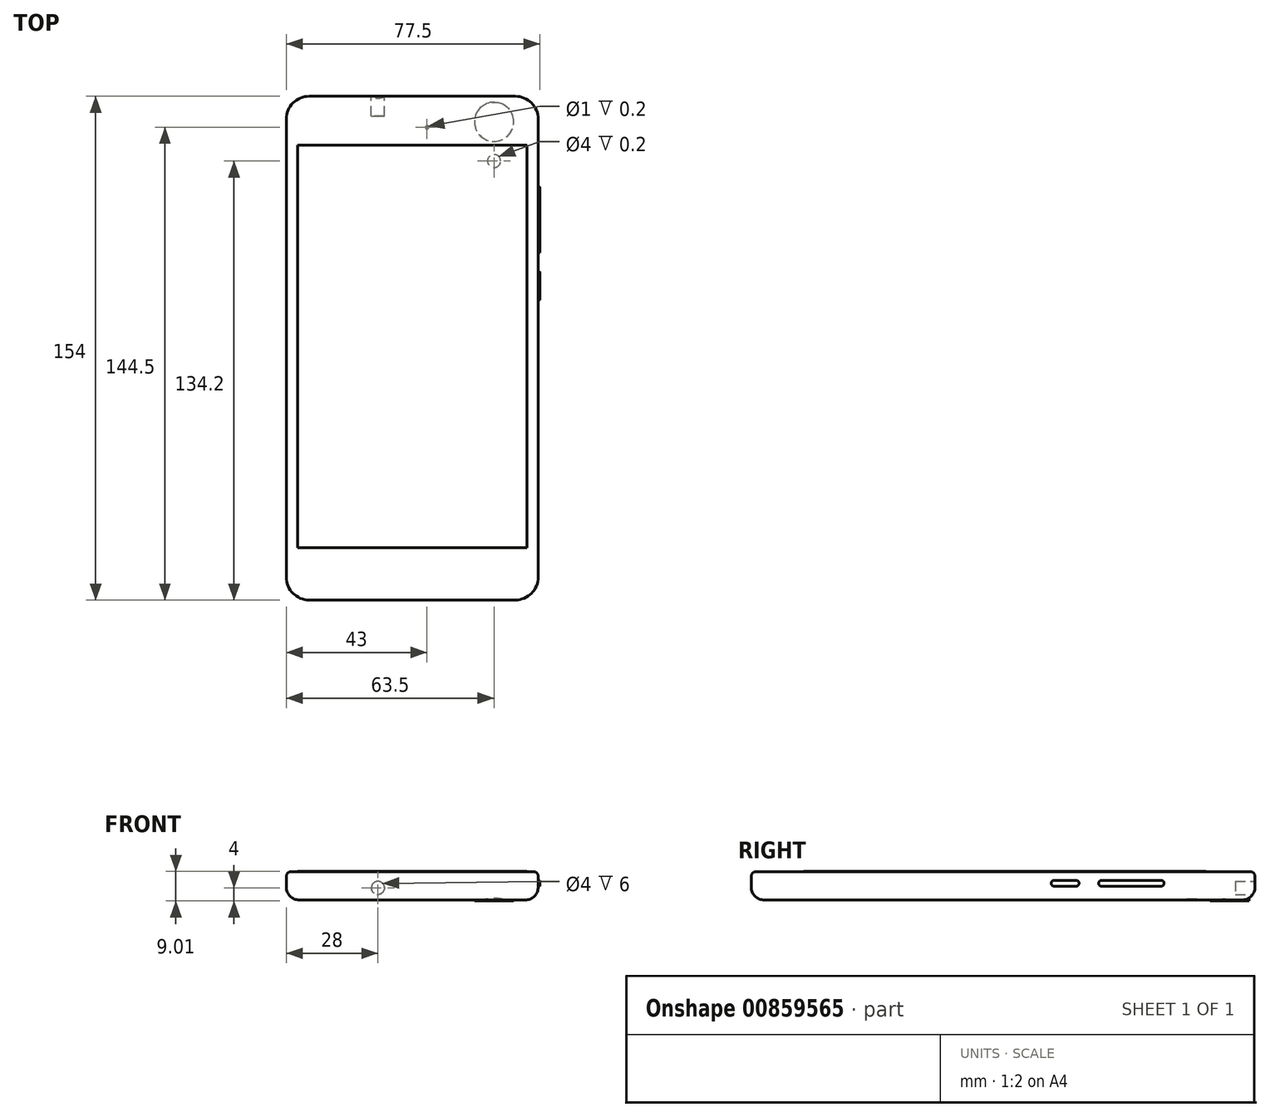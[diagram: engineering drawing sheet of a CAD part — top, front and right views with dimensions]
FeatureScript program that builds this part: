
annotation { "Feature Type Name" : "Feature", "Feature Type Description" : "" }
export const myFeature = defineFeature(function(context is Context, id is Id, definition is map)
    precondition{}
    {
        {
            var Q0;
            Q0=qCreatedBy(makeId("Top.planeOp"),FACE);
            var sketch = newSketch(context, id + "F0", { "sketchPlane" : qUnion([Q0])});
            skLineSegment(sketch, "E0.bottom", {"start": v(-31.5, 77) * mm, "end": v(31.5, 77) * mm});
            skLineSegment(sketch, "E0.top", {"start": v(-31.5, -77) * mm, "end": v(31.5, -77) * mm});
            skLineSegment(sketch, "E0.left", {"start": v(-38.5, 70) * mm, "end": v(-38.5, -70) * mm});
            skLineSegment(sketch, "E0.right", {"start": v(38.5, 70) * mm, "end": v(38.5, -70) * mm});
            skPoint(sketch, "E1.visualSharp", {"position": v(-38.5, 77) * mm});
            skArc(sketch, "E1.filletArc", {"start": v(-31.5, 77) * mm, "mid": v(-36.45, 74.95) * mm, "end": v(-38.5, 70) * mm});
            skPoint(sketch, "E2.visualSharp", {"position": v(-38.5, -77) * mm});
            skArc(sketch, "E2.filletArc", {"start": v(-38.5, -70) * mm, "mid": v(-36.45, -74.95) * mm, "end": v(-31.5, -77) * mm});
            skPoint(sketch, "E3.visualSharp", {"position": v(38.5, -77) * mm});
            skArc(sketch, "E3.filletArc", {"start": v(31.5, -77) * mm, "mid": v(36.45, -74.95) * mm, "end": v(38.5, -70) * mm});
            skPoint(sketch, "E4.visualSharp", {"position": v(38.5, 77) * mm});
            skArc(sketch, "E4.filletArc", {"start": v(38.5, 70) * mm, "mid": v(36.45, 74.95) * mm, "end": v(31.5, 77) * mm});
            skLineSegment(sketch, "E5", {"start": v(-38.5, 77) * mm, "end": v(38.5, -77) * mm, "construction": true});
            skSolve(sketch);
        }
        {
            var Q0;
            Q0=makeQuery(id+"F0.imprint","IMPRINT",FACE,{"disambiguationData":[TD([[makeQuery(id+"F0.imprint","IMPRINT",EDGE,{"derivedFrom":sQuery(id+"F0.wireOp",EDGE,"E0.bottom")}),-1.0]])]});
            extrude(context, id + "F1", {"entities" : qUnion([Q0]), "depth" : 8.7 * mm, "offsetDistance" : 25 * mm, "symmetric" : true});
        }
        {
            var Q0;
            Q0=makeQuery(id+"F1.opExtrude","CAP_EDGE",EDGE,{"disambiguationData":[OSD([sQuery(id+"F0.wireOp",EDGE,"E0.right")])],"isStart":true});
            fillet(context, id + "F2", {"entities" : qUnion([Q0]), "radius" : 4 * mm, "tangentPropagation" : true, "allowEdgeOverflow" : false});
        }
        {
            var Q0;
            Q0=makeQuery(id+"F1.opExtrude","CAP_FACE",FACE,{"disambiguationData":[OSD([sQuery(id+"F0.wireOp",EDGE,"E0.bottom"),sQuery(id+"F0.wireOp",EDGE,"E0.top"),sQuery(id+"F0.wireOp",EDGE,"E0.left"),sQuery(id+"F0.wireOp",EDGE,"E0.right"),sQuery(id+"F0.wireOp",EDGE,"E1.filletArc"),sQuery(id+"F0.wireOp",EDGE,"E2.filletArc"),sQuery(id+"F0.wireOp",EDGE,"E3.filletArc"),sQuery(id+"F0.wireOp",EDGE,"E4.filletArc")])],"isStart":false});
            fillet(context, id + "F3", {"entities" : qUnion([Q0]), "radius" : 1.5 * mm, "tangentPropagation" : true, "allowEdgeOverflow" : false});
        }
        {
            var Q0;
            Q0=makeQuery(id+"F1.opExtrude","CAP_FACE",FACE,{"disambiguationData":[OSD([sQuery(id+"F0.wireOp",EDGE,"E0.bottom"),sQuery(id+"F0.wireOp",EDGE,"E0.top"),sQuery(id+"F0.wireOp",EDGE,"E0.left"),sQuery(id+"F0.wireOp",EDGE,"E0.right"),sQuery(id+"F0.wireOp",EDGE,"E1.filletArc"),sQuery(id+"F0.wireOp",EDGE,"E2.filletArc"),sQuery(id+"F0.wireOp",EDGE,"E3.filletArc"),sQuery(id+"F0.wireOp",EDGE,"E4.filletArc")])],"isStart":true});
            cPlane(context, id + "F4", {"entities" : qUnion([Q0]), "cplaneType" : CPlaneType.OFFSET, "offset" : 0.3 * mm, "width" : 150 * mm, "height" : 150 * mm});
        }
        {
            var Q0;
            Q0=makeQuery(id+"F1.opExtrude","CAP_FACE",FACE,{"disambiguationData":[OSD([sQuery(id+"F0.wireOp",EDGE,"E0.bottom"),sQuery(id+"F0.wireOp",EDGE,"E0.top"),sQuery(id+"F0.wireOp",EDGE,"E0.left"),sQuery(id+"F0.wireOp",EDGE,"E0.right"),sQuery(id+"F0.wireOp",EDGE,"E1.filletArc"),sQuery(id+"F0.wireOp",EDGE,"E2.filletArc"),sQuery(id+"F0.wireOp",EDGE,"E3.filletArc"),sQuery(id+"F0.wireOp",EDGE,"E4.filletArc")])],"isStart":false});
            var sketch = newSketch(context, id + "F5", { "sketchPlane" : qUnion([Q0])});
            skLineSegment(sketch, "E6.0", {"start": v(-38.5, -70) * mm, "end": v(-38.5, 70) * mm});
            skLineSegment(sketch, "E7.0", {"start": v(31.5, -77) * mm, "end": v(-31.5, -77) * mm});
            skLineSegment(sketch, "E8.0", {"start": v(38.5, 70) * mm, "end": v(38.5, -70) * mm});
            skLineSegment(sketch, "E9.0", {"start": v(-31.5, 77) * mm, "end": v(31.5, 77) * mm});
            skSolve(sketch);
        }
        {
            var Q0;
            Q0=makeQuery(id+"F1.opExtrude","CAP_FACE",FACE,{"disambiguationData":[OSD([sQuery(id+"F0.wireOp",EDGE,"E0.bottom"),sQuery(id+"F0.wireOp",EDGE,"E0.top"),sQuery(id+"F0.wireOp",EDGE,"E0.left"),sQuery(id+"F0.wireOp",EDGE,"E0.right"),sQuery(id+"F0.wireOp",EDGE,"E1.filletArc"),sQuery(id+"F0.wireOp",EDGE,"E2.filletArc"),sQuery(id+"F0.wireOp",EDGE,"E3.filletArc"),sQuery(id+"F0.wireOp",EDGE,"E4.filletArc")])],"isStart":true});
            var sketch = newSketch(context, id + "F6", { "sketchPlane" : qUnion([Q0])});
            skLineSegment(sketch, "E10.0", {"start": v(31.5, -77) * mm, "end": v(-31.5, -77) * mm});
            skLineSegment(sketch, "E11.0", {"start": v(38.5, 70) * mm, "end": v(38.5, -70) * mm});
            skLineSegment(sketch, "E12", {"start": v(38.5, -70) * mm, "end": v(38.5, -77) * mm, "construction": true});
            skLineSegment(sketch, "E13", {"start": v(38.5, -77) * mm, "end": v(31.5, -77) * mm, "construction": true});
            skSolve(sketch);
        }
        {
            var Q0;
            Q0=qCreatedBy(id+"F4.planeOp",FACE);
            var sketch = newSketch(context, id + "F7", { "sketchPlane" : qUnion([Q0])});
            skCircle(sketch, "E14", {"center": v(25, -69.2) * mm, "radius": 6 * mm});
            skSolve(sketch);
        }
        {
            var Q0;
            Q0=makeQuery(id+"F7.imprint","IMPRINT",FACE,{"disambiguationData":[TD([[makeQuery(id+"F7.imprint","IMPRINT",EDGE,{"derivedFrom":sQuery(id+"F7.wireOp",EDGE,"E14")}),1.0]])]});
            var Q1;
            Q1=qCreatedBy(makeId("Top.planeOp"),FACE);
            extrude(context, id + "F8", {"entities" : qUnion([Q0]), "operationType" : NewBodyOperationType.ADD, "endBound" : BoundingType.UP_TO_SURFACE, "oppositeDirection" : true, "depth" : 25 * mm, "endBoundEntityFace" : qUnion([Q1]), "offsetDistance" : 25 * mm});
        }
        {
            var Q0;
            {var subQ0=sQuery(id+"F0.wireOp",EDGE,"E4.filletArc");var subQ1=sQuery(id+"F0.wireOp",EDGE,"E3.filletArc");var subQ2=sQuery(id+"F0.wireOp",EDGE,"E2.filletArc");var subQ3=sQuery(id+"F0.wireOp",EDGE,"E1.filletArc");var subQ4=sQuery(id+"F0.wireOp",EDGE,"E0.right");var subQ5=sQuery(id+"F0.wireOp",EDGE,"E0.left");var subQ6=sQuery(id+"F0.wireOp",EDGE,"E0.top");var subQ7=sQuery(id+"F0.wireOp",EDGE,"E0.bottom");var subQ8=makeQuery(id+"F1.opExtrude","CAP_FACE",FACE,{"disambiguationData":[OSD([subQ7,subQ6,subQ5,subQ4,subQ3,subQ2,subQ1,subQ0])],"isStart":false});Q0=makeQuery(id+"F5.imprint","IMPRINT",FACE,{"disambiguationData":[TD([[makeQuery(id+"F5.imprint","IMPRINT",EDGE,{"derivedFrom":makeQuery(id+"F3.opFillet","BLEND_EDGE",EDGE,{"blendedFrom":[makeQuery(id+"F1.opExtrude","CAP_EDGE",EDGE,{"disambiguationData":[OSD([subQ7])],"isStart":false}),subQ8],"blendedInto":[subQ8]})}),1.0]])]});}
            var sketch = newSketch(context, id + "F9", { "sketchPlane" : qUnion([Q0])});
            skLineSegment(sketch, "E15.bottom", {"start": v(-35.1, 62) * mm, "end": v(35.1, 62) * mm});
            skLineSegment(sketch, "E15.top", {"start": v(-35.1, -61) * mm, "end": v(35.1, -61) * mm});
            skLineSegment(sketch, "E15.left", {"start": v(-35.1, 62) * mm, "end": v(-35.1, -61) * mm});
            skLineSegment(sketch, "E15.right", {"start": v(35.1, 62) * mm, "end": v(35.1, -61) * mm});
            skSolve(sketch);
        }
        {
            var Q0;
            Q0=makeQuery(id+"F9.imprint","IMPRINT",FACE,{"disambiguationData":[TD([[makeQuery(id+"F9.imprint","IMPRINT",EDGE,{"derivedFrom":sQuery(id+"F9.wireOp",EDGE,"E15.bottom")}),-1.0]])]});
            var Q1;
            Q1=sQuery(id+"F9.wireOp",EDGE,"E15.bottom");
            var Q2;
            Q2=sQuery(id+"F9.wireOp",EDGE,"E15.left");
            var Q3;
            Q3=sQuery(id+"F9.wireOp",EDGE,"E15.top");
            var Q4;
            Q4=sQuery(id+"F9.wireOp",EDGE,"E15.right");
            extrude(context, id + "F10", {"entities" : qUnion([Q0]), "surfaceOperationType" : NewSurfaceOperationType.ADD, "surfaceEntities" : qUnion([Q1, Q2, Q3, Q4]), "depth" : 0.01 * mm, "offsetDistance" : 25 * mm});
        }
        {
            var Q0;
            {var subQ0=sQuery(id+"F0.wireOp",EDGE,"E4.filletArc");var subQ1=sQuery(id+"F0.wireOp",EDGE,"E3.filletArc");var subQ2=sQuery(id+"F0.wireOp",EDGE,"E2.filletArc");var subQ3=sQuery(id+"F0.wireOp",EDGE,"E1.filletArc");var subQ4=sQuery(id+"F0.wireOp",EDGE,"E0.right");var subQ5=sQuery(id+"F0.wireOp",EDGE,"E0.left");var subQ6=sQuery(id+"F0.wireOp",EDGE,"E0.top");var subQ7=sQuery(id+"F0.wireOp",EDGE,"E0.bottom");var subQ8=makeQuery(id+"F1.opExtrude","CAP_FACE",FACE,{"disambiguationData":[OSD([subQ7,subQ6,subQ5,subQ4,subQ3,subQ2,subQ1,subQ0])],"isStart":true});Q0=makeQuery(id+"F6.imprint","IMPRINT",FACE,{"disambiguationData":[TD([[makeQuery(id+"F6.imprint","IMPRINT",EDGE,{"derivedFrom":makeQuery(id+"F2.opFillet","BLEND_EDGE",EDGE,{"blendedFrom":[makeQuery(id+"F1.opExtrude","CAP_EDGE",EDGE,{"disambiguationData":[OSD([subQ7])],"isStart":true}),subQ8],"blendedInto":[subQ8]})}),1.0]])]});}
            var sketch = newSketch(context, id + "F11", { "sketchPlane" : qUnion([Q0])});
            skCircle(sketch, "E16", {"center": v(25, -57.2) * mm, "radius": 2 * mm});
            skCircle(sketch, "E17.0", {"center": v(25, -69.2) * mm, "radius": 6 * mm});
            skCircle(sketch, "E18", {"center": v(4.5, -67.5) * mm, "radius": 0.5 * mm});
            skSolve(sketch);
        }
        {
            var Q0;
            Q0=makeQuery(id+"F11.imprint","IMPRINT",FACE,{"disambiguationData":[TD([[makeQuery(id+"F11.imprint","IMPRINT",EDGE,{"derivedFrom":sQuery(id+"F11.wireOp",EDGE,"E16")}),1.0]])]});
            var Q1;
            Q1=makeQuery(id+"F11.imprint","IMPRINT",FACE,{"disambiguationData":[TD([[makeQuery(id+"F11.imprint","IMPRINT",EDGE,{"derivedFrom":sQuery(id+"F11.wireOp",EDGE,"E18")}),1.0]])]});
            extrude(context, id + "F12", {"entities" : qUnion([Q0, Q1]), "operationType" : NewBodyOperationType.REMOVE, "oppositeDirection" : true, "depth" : 0.2 * mm, "offsetDistance" : 25 * mm});
        }
        {
            var Q0;
            Q0=makeQuery(id+"F1.opExtrude","SWEPT_FACE",FACE,{"disambiguationData":[OSD([sQuery(id+"F0.wireOp",EDGE,"E0.bottom")])]});
            var sketch = newSketch(context, id + "F13", { "sketchPlane" : qUnion([Q0])});
            skCircle(sketch, "E19", {"center": v(10.5, -0.65) * mm, "radius": 2 * mm});
            skSolve(sketch);
        }
        {
            var Q0;
            {var subQ0=sQuery(id+"F13.wireOp",EDGE,"E19");var subQ1=sQuery(id+"F0.wireOp",EDGE,"E0.bottom");var subQ2=makeQuery(id+"F2.opFillet","BLEND_EDGE",EDGE,{"blendedFrom":[makeQuery(id+"F1.opExtrude","CAP_EDGE",EDGE,{"disambiguationData":[OSD([subQ1])],"isStart":true}),makeQuery(id+"F1.opExtrude","SWEPT_FACE",FACE,{"disambiguationData":[OSD([subQ1])]})],"blendedInto":[makeQuery(id+"F1.opExtrude","SWEPT_FACE",FACE,{"disambiguationData":[OSD([subQ1])]})]});var subQ3=makeQuery(id+"F13.imprint","INTERSECT",VERTEX,{"disambiguationData":[OD(0.0)],"derivedFrom":[subQ2,subQ0]});Q0=makeQuery(id+"F13.imprint","IMPRINT",FACE,{"disambiguationData":[TD([[makeQuery(id+"F13.imprint","IMPRINT",EDGE,{"disambiguationData":[TD([[subQ3,-1.0]])],"derivedFrom":subQ0}),1.0]])]});}
            var Q1;
            {var subQ0=sQuery(id+"F13.wireOp",EDGE,"E19");var subQ1=sQuery(id+"F0.wireOp",EDGE,"E0.bottom");var subQ2=makeQuery(id+"F2.opFillet","BLEND_EDGE",EDGE,{"blendedFrom":[makeQuery(id+"F1.opExtrude","CAP_EDGE",EDGE,{"disambiguationData":[OSD([subQ1])],"isStart":true}),makeQuery(id+"F1.opExtrude","SWEPT_FACE",FACE,{"disambiguationData":[OSD([subQ1])]})],"blendedInto":[makeQuery(id+"F1.opExtrude","SWEPT_FACE",FACE,{"disambiguationData":[OSD([subQ1])]})]});var subQ3=makeQuery(id+"F13.imprint","INTERSECT",VERTEX,{"disambiguationData":[OD(0.0)],"derivedFrom":[subQ2,subQ0]});Q1=makeQuery(id+"F13.imprint","IMPRINT",FACE,{"disambiguationData":[TD([[makeQuery(id+"F13.imprint","IMPRINT",EDGE,{"disambiguationData":[TD([[subQ3,1.0]])],"derivedFrom":subQ0}),1.0]])]});}
            extrude(context, id + "F14", {"entities" : qUnion([Q0, Q1]), "operationType" : NewBodyOperationType.REMOVE, "oppositeDirection" : true, "depth" : 6 * mm, "offsetDistance" : 25 * mm});
        }
        {
            var Q0;
            Q0=makeQuery(id+"F1.opExtrude","SWEPT_FACE",FACE,{"disambiguationData":[OSD([sQuery(id+"F0.wireOp",EDGE,"E0.right")])]});
            var sketch = newSketch(context, id + "F15", { "sketchPlane" : qUnion([Q0])});
            skLineSegment(sketch, "E20.bottom", {"start": v(30.1, 1.65) * mm, "end": v(48.3, 1.65) * mm});
            skLineSegment(sketch, "E20.top", {"start": v(30.1, -0.15) * mm, "end": v(48.3, -0.15) * mm});
            skLineSegment(sketch, "E20.left", {"start": v(30.1, 1.65) * mm, "end": v(30.1, -0.15) * mm});
            skLineSegment(sketch, "E20.right", {"start": v(48.3, 1.65) * mm, "end": v(48.3, -0.15) * mm});
            skArc(sketch, "E21", {"start": v(30.1, 1.65) * mm, "mid": v(29.2, 0.75) * mm, "end": v(30.1, -0.15) * mm});
            skArc(sketch, "E22", {"start": v(48.3, -0.15) * mm, "mid": v(49.2, 0.75) * mm, "end": v(48.3, 1.65) * mm});
            skLineSegment(sketch, "E23", {"start": v(49.2, 0.75) * mm, "end": v(29.2, 0.75) * mm, "construction": true});
            skLineSegment(sketch, "E24.bottom", {"start": v(15.6, 1.65) * mm, "end": v(22.3, 1.65) * mm});
            skLineSegment(sketch, "E24.top", {"start": v(15.6, -0.15) * mm, "end": v(22.3, -0.15) * mm});
            skLineSegment(sketch, "E24.left", {"start": v(15.6, 1.65) * mm, "end": v(15.6, -0.15) * mm});
            skLineSegment(sketch, "E24.right", {"start": v(22.3, 1.65) * mm, "end": v(22.3, -0.15) * mm});
            skArc(sketch, "E25", {"start": v(22.3, -0.15) * mm, "mid": v(23.2, 0.75) * mm, "end": v(22.3, 1.65) * mm});
            skArc(sketch, "E26", {"start": v(15.6, 1.65) * mm, "mid": v(14.7, 0.75) * mm, "end": v(15.6, -0.15) * mm});
            skLineSegment(sketch, "E27", {"start": v(23.2, 0.75) * mm, "end": v(14.7, 0.75) * mm, "construction": true});
            skSolve(sketch);
        }
        {
            var Q0;
            Q0=makeQuery(id+"F15.imprint","IMPRINT",FACE,{"disambiguationData":[TD([[makeQuery(id+"F15.imprint","IMPRINT",EDGE,{"derivedFrom":sQuery(id+"F15.wireOp",EDGE,"E20.right")}),1.0]])]});
            var Q1;
            Q1=makeQuery(id+"F15.imprint","IMPRINT",FACE,{"disambiguationData":[TD([[makeQuery(id+"F15.imprint","IMPRINT",EDGE,{"derivedFrom":sQuery(id+"F15.wireOp",EDGE,"E20.bottom")}),-1.0]])]});
            var Q2;
            Q2=makeQuery(id+"F15.imprint","IMPRINT",FACE,{"disambiguationData":[TD([[makeQuery(id+"F15.imprint","IMPRINT",EDGE,{"derivedFrom":sQuery(id+"F15.wireOp",EDGE,"E20.left")}),-1.0]])]});
            var Q3;
            Q3=makeQuery(id+"F15.imprint","IMPRINT",FACE,{"disambiguationData":[TD([[makeQuery(id+"F15.imprint","IMPRINT",EDGE,{"derivedFrom":sQuery(id+"F15.wireOp",EDGE,"E24.right")}),1.0]])]});
            var Q4;
            Q4=makeQuery(id+"F15.imprint","IMPRINT",FACE,{"disambiguationData":[TD([[makeQuery(id+"F15.imprint","IMPRINT",EDGE,{"derivedFrom":sQuery(id+"F15.wireOp",EDGE,"E24.bottom")}),-1.0]])]});
            var Q5;
            Q5=makeQuery(id+"F15.imprint","IMPRINT",FACE,{"disambiguationData":[TD([[makeQuery(id+"F15.imprint","IMPRINT",EDGE,{"derivedFrom":sQuery(id+"F15.wireOp",EDGE,"E24.left")}),-1.0]])]});
            extrude(context, id + "F16", {"entities" : qUnion([Q0, Q1, Q2, Q3, Q4, Q5]), "operationType" : NewBodyOperationType.ADD, "depth" : 0.5 * mm, "offsetDistance" : 25 * mm});
        }
    });
